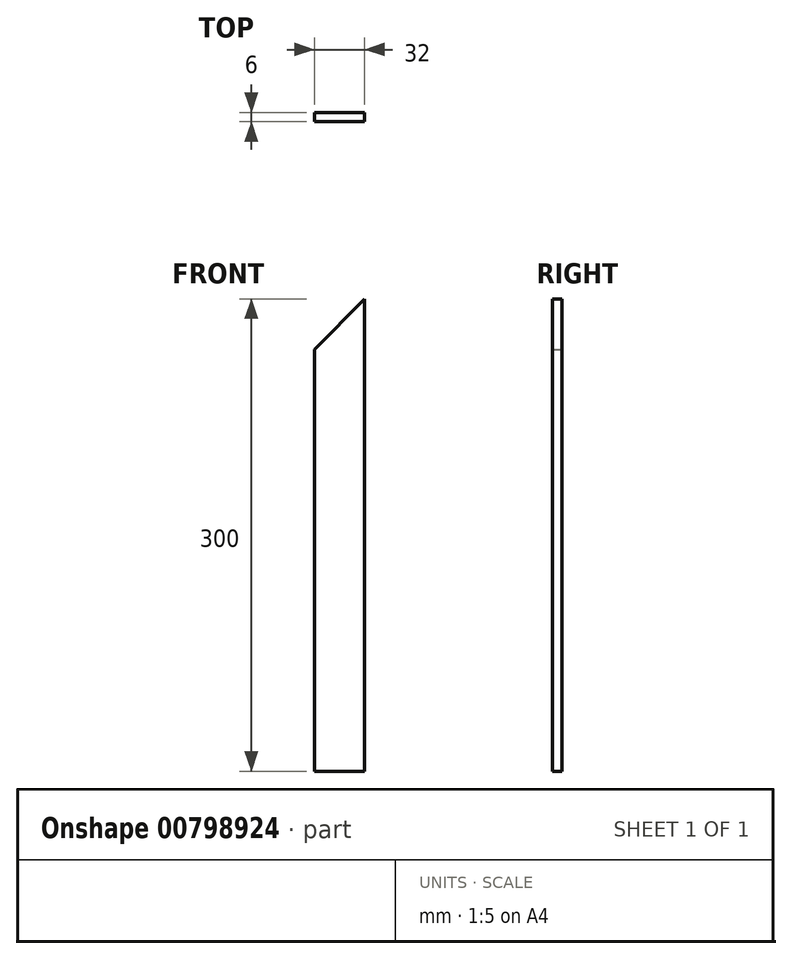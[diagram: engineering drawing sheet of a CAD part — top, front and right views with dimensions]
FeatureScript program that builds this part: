
annotation { "Feature Type Name" : "Feature", "Feature Type Description" : "" }
export const myFeature = defineFeature(function(context is Context, id is Id, definition is map)
    precondition{}
    {
        {
            var Q0;
            Q0=qCreatedBy(makeId("Front.planeOp"),FACE);
            var sketch = newSketch(context, id + "F0", { "sketchPlane" : qUnion([Q0])});
            skLineSegment(sketch, "E0", {"start": v(0, 0) * mm, "end": v(0, -300) * mm});
            skLineSegment(sketch, "E1", {"start": v(0, -300) * mm, "end": v(-32, -300) * mm});
            skLineSegment(sketch, "E2", {"start": v(0, 0) * mm, "end": v(-32, -32) * mm});
            skLineSegment(sketch, "E3", {"start": v(-32, -32) * mm, "end": v(-32, -300) * mm});
            skSolve(sketch);
        }
        {
            var Q0;
            Q0=makeQuery(id+"F0.imprint","IMPRINT",FACE,{"disambiguationData":[TD([[makeQuery(id+"F0.imprint","IMPRINT",EDGE,{"derivedFrom":sQuery(id+"F0.wireOp",EDGE,"E0")}),-1.0]])]});
            extrude(context, id + "F1", {"entities" : qUnion([Q0]), "endBound" : BoundingType.SYMMETRIC, "depth" : 6 * mm});
        }
    });
